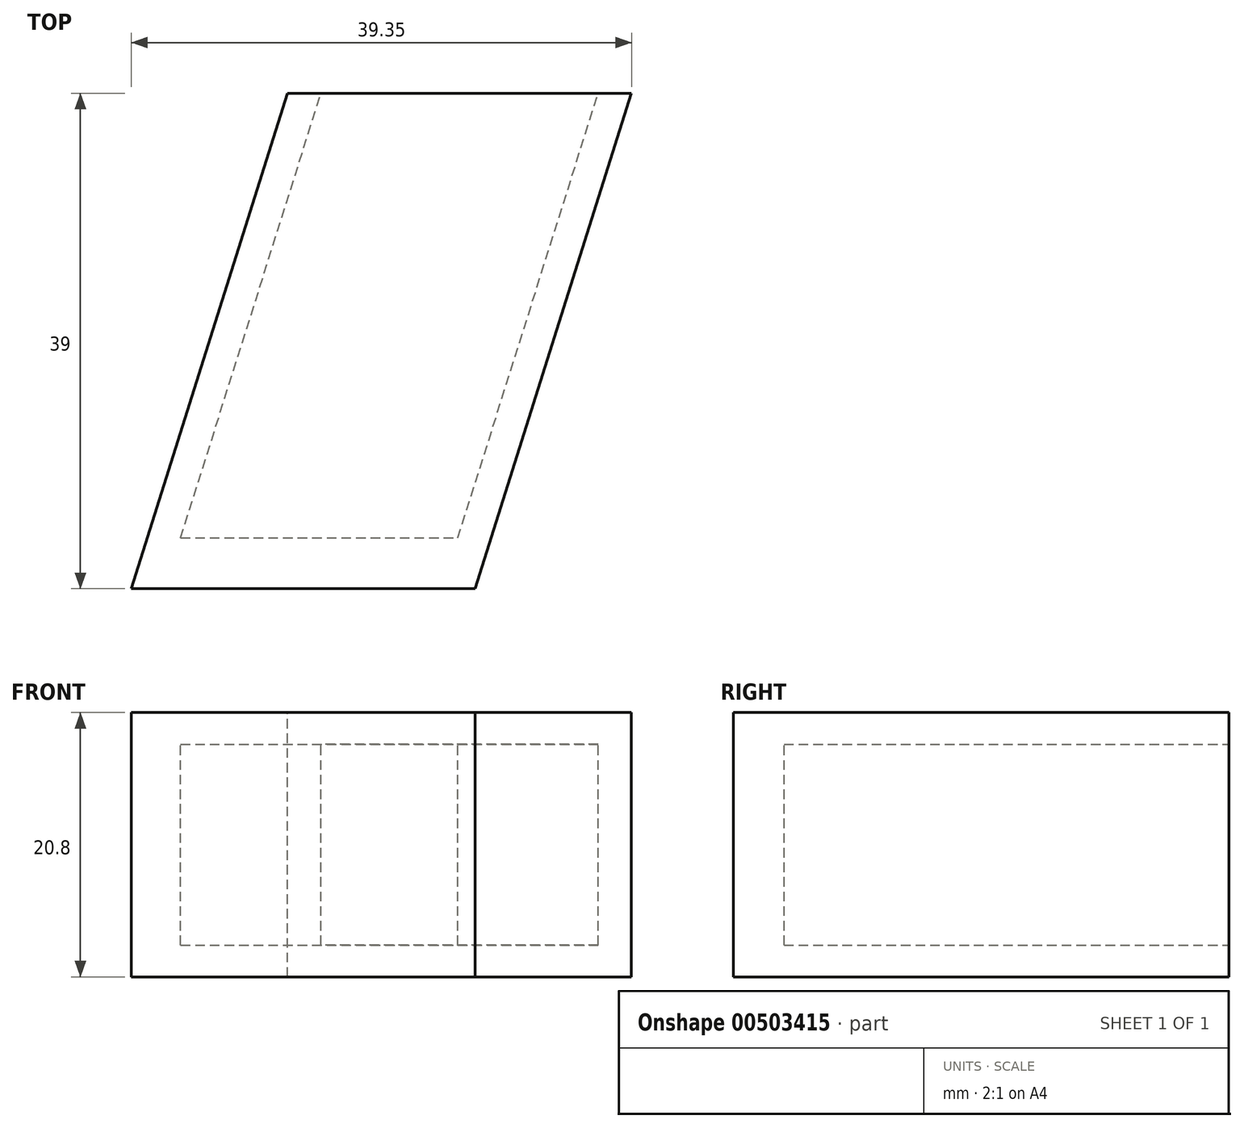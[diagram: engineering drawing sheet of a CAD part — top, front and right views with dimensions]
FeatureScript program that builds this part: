
annotation { "Feature Type Name" : "Feature", "Feature Type Description" : "" }
export const myFeature = defineFeature(function(context is Context, id is Id, definition is map)
    precondition{}
    {
        {
            var Q0;
            Q0=qCreatedBy(makeId("Top.planeOp"),FACE);
            var sketch = newSketch(context, id + "F0", { "sketchPlane" : qUnion([Q0])});
            skLineSegment(sketch, "E0", {"start": v(0, 0) * mm, "end": v(21.8, 0) * mm});
            skLineSegment(sketch, "E1", {"start": v(0, 0) * mm, "end": v(11.04, 35) * mm});
            skLineSegment(sketch, "E2.0", {"start": v(-3.88, -4) * mm, "end": v(8.41, 35) * mm});
            skLineSegment(sketch, "E3.0", {"start": v(21.8, 0) * mm, "end": v(32.84, 35) * mm});
            skLineSegment(sketch, "E4.0", {"start": v(23.17, -4) * mm, "end": v(35.47, 35) * mm});
            skLineSegment(sketch, "E5.0", {"start": v(-3.88, -4) * mm, "end": v(23.17, -4) * mm});
            skLineSegment(sketch, "E6.0", {"start": v(8.41, 35) * mm, "end": v(11.04, 35) * mm});
            skLineSegment(sketch, "E7.trimOffspring", {"start": v(32.84, 35) * mm, "end": v(35.47, 35) * mm});
            skPoint(sketch, "E8.start.orphan", {"position": v(0, 44.88) * mm});
            skSolve(sketch);
        }
        {
            var Q0;
            Q0=makeQuery(id+"F0.imprint","IMPRINT",FACE,{"disambiguationData":[TD([[makeQuery(id+"F0.imprint","IMPRINT",EDGE,{"derivedFrom":sQuery(id+"F0.wireOp",EDGE,"E0")}),-1.0]])]});
            extrude(context, id + "F1", {"entities" : qUnion([Q0]), "oppositeDirection" : true, "depth" : 15.8 * mm});
        }
        {
            var Q0;
            Q0=makeQuery(id+"F1.opExtrude","CAP_FACE",FACE,{"disambiguationData":[OSD([sQuery(id+"F0.wireOp",EDGE,"E0"),sQuery(id+"F0.wireOp",EDGE,"E1"),sQuery(id+"F0.wireOp",EDGE,"E2.0"),sQuery(id+"F0.wireOp",EDGE,"E3.0"),sQuery(id+"F0.wireOp",EDGE,"E4.0"),sQuery(id+"F0.wireOp",EDGE,"E5.0"),sQuery(id+"F0.wireOp",EDGE,"E6.0"),sQuery(id+"F0.wireOp",EDGE,"E7.trimOffspring")])],"isStart":false});
            var sketch = newSketch(context, id + "F2", { "sketchPlane" : qUnion([Q0])});
            skLineSegment(sketch, "E9", {"start": v(35.47, -35) * mm, "end": v(8.41, -35) * mm});
            skLineSegment(sketch, "E10", {"start": v(8.41, -35) * mm, "end": v(-3.88, 4) * mm});
            skLineSegment(sketch, "E11", {"start": v(-3.88, 4) * mm, "end": v(23.17, 4) * mm});
            skLineSegment(sketch, "E12", {"start": v(23.17, 4) * mm, "end": v(35.47, -35) * mm});
            skSolve(sketch);
        }
        {
            var Q0;
            Q0=makeQuery(id+"F2.imprint","IMPRINT",FACE,{"disambiguationData":[TD([[makeQuery(id+"F2.imprint","IMPRINT",EDGE,{"derivedFrom":makeQuery(id+"F1.opExtrude","CAP_EDGE",EDGE,{"disambiguationData":[OSD([sQuery(id+"F0.wireOp",EDGE,"E0")])],"isStart":false})}),-1.0]])]});
            var Q1;
            {var subQ0=sQuery(id+"F2.wireOp",EDGE,"E10");Q1=makeQuery(id+"F2.imprint","IMPRINT",FACE,{"disambiguationData":[TD([[makeQuery(id+"F2.imprint","IMPRINT",EDGE,{"derivedFrom":subQ0}),1.0]])]});}
            extrude(context, id + "F3", {"entities" : qUnion([Q0, Q1]), "operationType" : NewBodyOperationType.ADD, "depth" : 2.5 * mm});
        }
        {
            var Q0;
            Q0=makeQuery(id+"F3.opExtrude","CAP_FACE",FACE,{"disambiguationData":[OSD([sQuery(id+"F2.wireOp",EDGE,"E9"),sQuery(id+"F2.wireOp",EDGE,"E10"),sQuery(id+"F2.wireOp",EDGE,"E11"),sQuery(id+"F2.wireOp",EDGE,"E12")])],"isStart":false});
            extrude(context, id + "F4", {"entities" : qUnion([Q0]), "operationType" : NewBodyOperationType.ADD, "oppositeDirection" : true, "depth" : (15.8 + 2.5 + 2.5) * mm, "hasSecondDirection" : true, "secondDirectionOppositeDirection" : true, "secondDirectionDepth" : (2.5 + 15.8) * mm});
        }
    });
